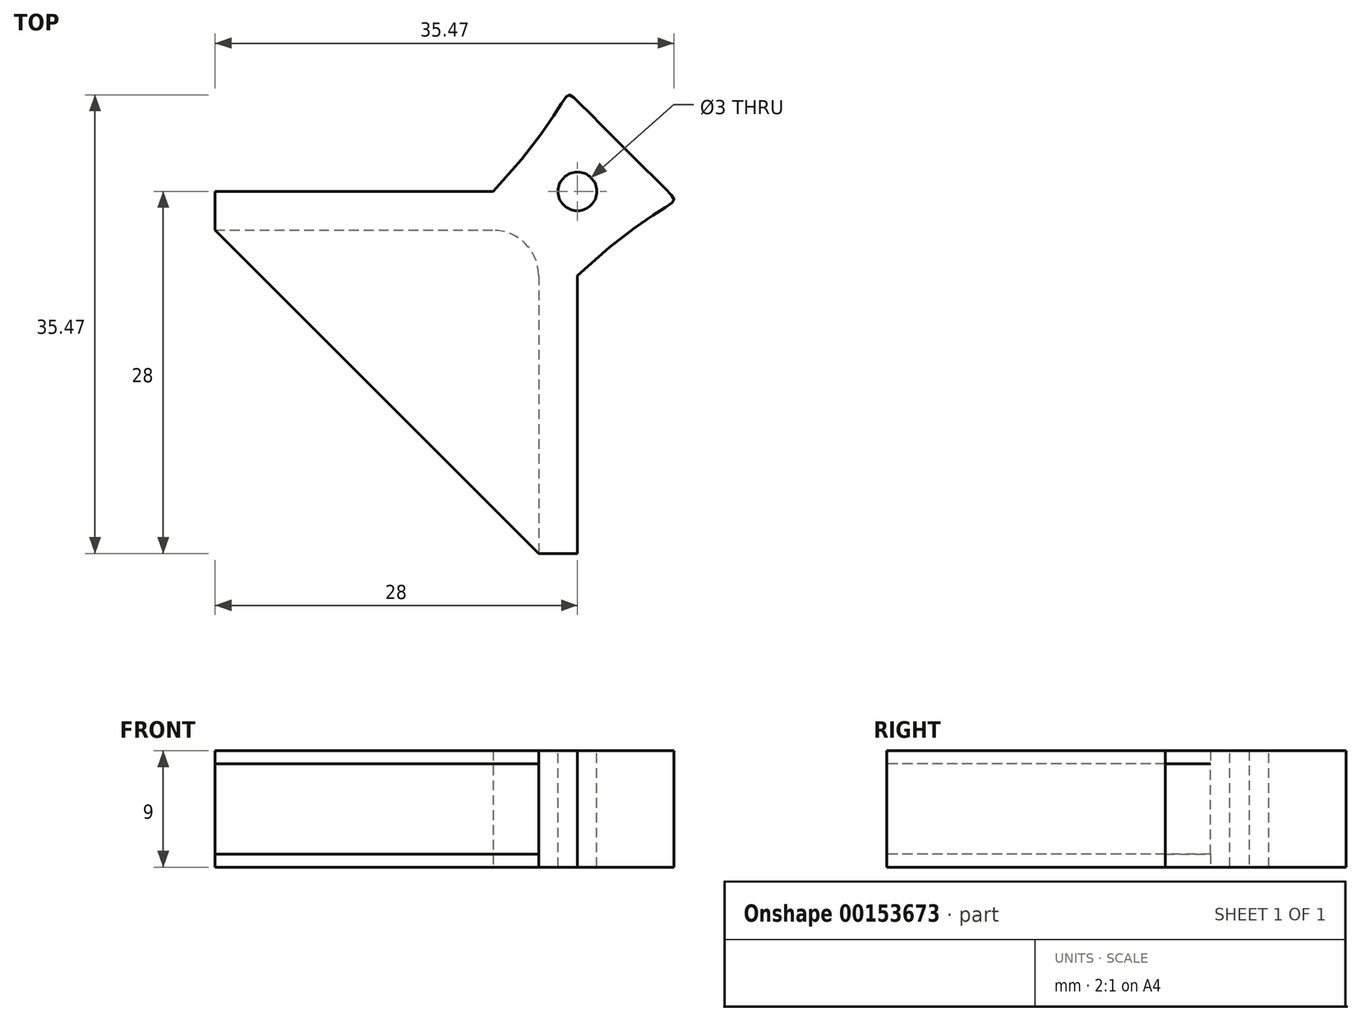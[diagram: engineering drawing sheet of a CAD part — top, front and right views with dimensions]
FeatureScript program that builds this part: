
annotation { "Feature Type Name" : "Feature", "Feature Type Description" : "" }
export const myFeature = defineFeature(function(context is Context, id is Id, definition is map)
    precondition{}
    {
        {
            var Q0;
            Q0=qCreatedBy(makeId("Top.planeOp"),FACE);
            var sketch = newSketch(context, id + "F0", { "sketchPlane" : qUnion([Q0])});
            skLineSegment(sketch, "E0", {"start": v(0, 0) * mm, "end": v(21.5, 0) * mm});
            skLineSegment(sketch, "E1", {"start": v(25, -3.5) * mm, "end": v(25, -25) * mm});
            skLineSegment(sketch, "E2", {"start": v(0, 0) * mm, "end": v(25, -25) * mm});
            skArc(sketch, "E3", {"start": v(25, -3.5) * mm, "mid": v(23.97, -1.03) * mm, "end": v(21.5, 0) * mm});
            skSolve(sketch);
        }
        {
            var Q0;
            Q0=makeQuery(id+"F0.imprint","IMPRINT",FACE,{"disambiguationData":[TD([[makeQuery(id+"F0.imprint","IMPRINT",EDGE,{"derivedFrom":sQuery(id+"F0.wireOp",EDGE,"E0")}),-1.0]])]});
            var sketch = newSketch(context, id + "F1", { "sketchPlane" : qUnion([Q0])});
            skLineSegment(sketch, "E4.0", {"start": v(28, -3.5) * mm, "end": v(28, -25) * mm});
            skArc(sketch, "E4.1", {"start": v(28, -3.5) * mm, "mid": v(26.1, 1.1) * mm, "end": v(21.5, 3) * mm});
            skLineSegment(sketch, "E4.2", {"start": v(0, 3) * mm, "end": v(21.5, 3) * mm});
            skLineSegment(sketch, "E5", {"start": v(0, 3) * mm, "end": v(0, 0) * mm});
            skLineSegment(sketch, "E6", {"start": v(0, 0) * mm, "end": v(25, -25) * mm});
            skLineSegment(sketch, "E7", {"start": v(25, -25) * mm, "end": v(28, -25) * mm});
            skSolve(sketch);
        }
        {
            var Q0;
            Q0 = qSketchRegion(id + "F1", true);
            extrude(context, id + "F2", {"entities" : qUnion([Q0]), "depth" : 4.5 * mm, "hasSecondDirection" : true, "secondDirectionOppositeDirection" : true, "secondDirectionDepth" : 4.5 * mm});
        }
        {
            var Q0;
            Q0 = qSketchRegion(id + "F0", true);
            extrude(context, id + "F3", {"entities" : qUnion([Q0]), "operationType" : NewBodyOperationType.REMOVE, "oppositeDirection" : true, "depth" : 3.5 * mm, "hasSecondDirection" : true, "secondDirectionOppositeDirection" : false, "secondDirectionDepth" : 3.5 * mm});
        }
        {
            var Q0;
            Q0=makeQuery(id+"F2.opExtrude","CAP_FACE",FACE,{"disambiguationData":[OSD([sQuery(id+"F1.wireOp",EDGE,"E4.0"),sQuery(id+"F1.wireOp",EDGE,"E4.1"),sQuery(id+"F1.wireOp",EDGE,"E4.2"),sQuery(id+"F1.wireOp",EDGE,"E5"),sQuery(id+"F1.wireOp",EDGE,"E6"),sQuery(id+"F1.wireOp",EDGE,"E7")])],"isStart":false});
            var sketch = newSketch(context, id + "F4", { "sketchPlane" : qUnion([Q0])});
            skLineSegment(sketch, "E8", {"start": v(28, -25) * mm, "end": v(28, 10) * mm, "construction": true});
            skLineSegment(sketch, "E9", {"start": v(0, 3) * mm, "end": v(35, 3) * mm, "construction": true});
            skFitSpline(sketch, "E10", {"points": [v(21.5, 3) * mm, v(28, 10) * mm, v(35, 3) * mm, v(28, -3.5) * mm], "startDerivative": vector(58.85, 63.38) * mm, "endDerivative": vector(-63.38, -58.85) * mm});
            skArc(sketch, "E11.0", {"start": v(28, -3.5) * mm, "mid": v(26.1, 1.1) * mm, "end": v(21.5, 3) * mm});
            skCircle(sketch, "E12", {"center": v(28, 3) * mm, "radius": 1.5 * mm});
            skSolve(sketch);
        }
        {
            var Q0;
            Q0=makeQuery(id+"F4.imprint","IMPRINT",FACE,{"disambiguationData":[TD([[makeQuery(id+"F4.imprint","IMPRINT",EDGE,{"derivedFrom":sQuery(id+"F4.wireOp",EDGE,"E10")}),-1.0]])]});
            var Q1;
            Q1=makeQuery(id+"F2.opExtrude","CAP_FACE",FACE,{"disambiguationData":[OSD([sQuery(id+"F1.wireOp",EDGE,"E4.0"),sQuery(id+"F1.wireOp",EDGE,"E4.1"),sQuery(id+"F1.wireOp",EDGE,"E4.2"),sQuery(id+"F1.wireOp",EDGE,"E5"),sQuery(id+"F1.wireOp",EDGE,"E6"),sQuery(id+"F1.wireOp",EDGE,"E7")])],"isStart":true});
            extrude(context, id + "F5", {"entities" : qUnion([Q0]), "operationType" : NewBodyOperationType.ADD, "endBound" : BoundingType.UP_TO_SURFACE, "oppositeDirection" : true, "endBoundEntityFace" : qUnion([Q1]), "depth" : 25 * mm});
        }
    });
